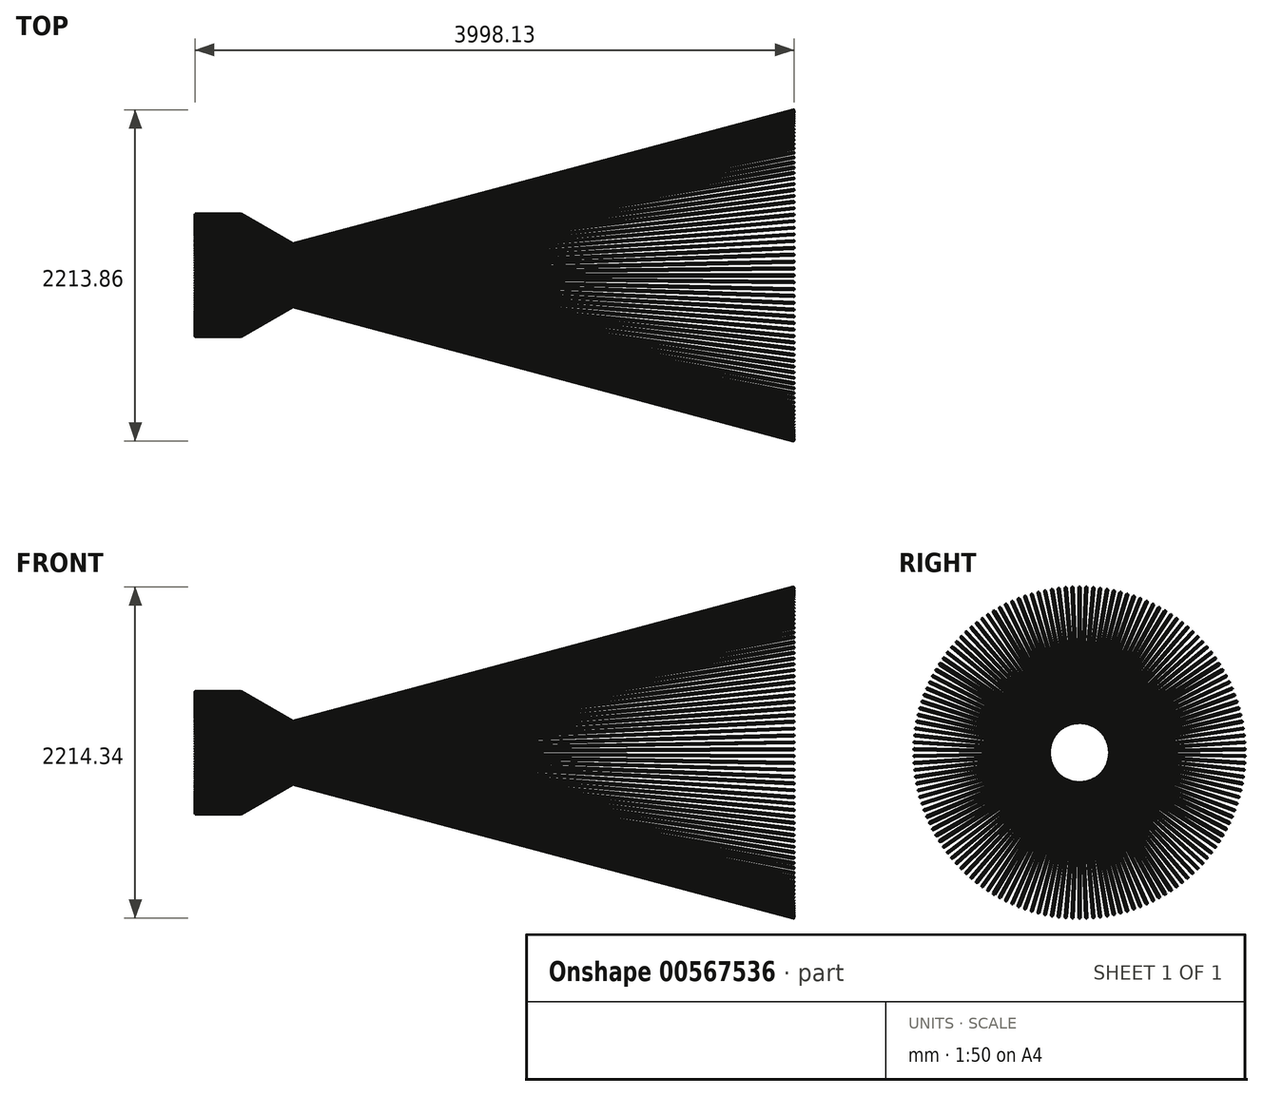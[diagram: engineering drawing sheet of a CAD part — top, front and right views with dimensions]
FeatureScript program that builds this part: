
annotation { "Feature Type Name" : "Feature", "Feature Type Description" : "" }
export const myFeature = defineFeature(function(context is Context, id is Id, definition is map)
    precondition{}
    {
        {
            var Q0;
            Q0=qCreatedBy(makeId("Right.planeOp"),FACE);
            var sketch = newSketch(context, id + "F0", { "sketchPlane" : qUnion([Q0])});
            skCircle(sketch, "E0", {"center": v(0, 405.5) * mm, "radius": 4.37 * mm});
            skSolve(sketch);
        }
        {
            var Q0;
            Q0=qCreatedBy(makeId("Front.planeOp"),FACE);
            var sketch = newSketch(context, id + "F1", { "sketchPlane" : qUnion([Q0])});
            skLineSegment(sketch, "E1", {"start": v(0, 400.9) * mm, "end": v(300, 400.9) * mm});
            skLineSegment(sketch, "E2", {"start": v(300, 400.9) * mm, "end": v(647, 200.56) * mm});
            skLineSegment(sketch, "E3", {"start": v(3998.18, 1098.5) * mm, "end": v(647, 200.56) * mm});
            skSolve(sketch);
        }
        {
            var Q0;
            Q0=makeQuery(id+"F0.imprint","IMPRINT",FACE,{"disambiguationData":[TD([[makeQuery(id+"F0.imprint","IMPRINT",EDGE,{"derivedFrom":sQuery(id+"F0.wireOp",EDGE,"E0")}),1.0]])]});
            var Q1;
            Q1=sQuery(id+"F1.wireOp",EDGE,"E1");
            var Q2;
            Q2=sQuery(id+"F1.wireOp",EDGE,"E2");
            var Q3;
            Q3=sQuery(id+"F1.wireOp",EDGE,"E3");
            sweep(context, id + "F2", {"profiles" : qUnion([Q0]), "path" : qUnion([Q1, Q2, Q3])});
        }
        {
            var Q0;
            Q0=qCreatedBy(makeId("Front.planeOp"),FACE);
            var sketch = newSketch(context, id + "F3", { "sketchPlane" : qUnion([Q0])});
            skLineSegment(sketch, "E4", {"start": v(0, 0) * mm, "end": v(74.42, 0) * mm});
            skSolve(sketch);
        }
        {
            var Q0;
            Q0=makeQuery(id+"F2.opSweep","SWEPT_BODY",BODY,{"disambiguationData":[OSD([sQuery(id+"F0.wireOp",EDGE,"E0"),sQuery(id+"F1.wireOp",EDGE,"E3")])]});
            var Q1;
            Q1=sQuery(id+"F3.wireOp",EDGE,"E4");
            circularPattern(context, id + "F4", {"entities" : qUnion([Q0]), "axis" : qUnion([Q1]), "angle" : 360 * degree, "instanceCount" : 150, "equalSpace" : true});
        }
        {
            var Q0;
            Q0 = qSketchRegion(id + "F1", true);
            var Q1;
            Q1 = qConstructionFilter(qBodyType(qCreatedBy(id + "F1" ,EDGE), BodyType.WIRE), ConstructionObject.NO);
            var Q2;
            Q2=sQuery(id+"F3.wireOp",EDGE,"E4");
            revolve(context, id + "F5", {"bodyType" : ToolBodyType.SURFACE, "entities" : qUnion([Q0]), "surfaceEntities" : qUnion([Q1]), "axis" : qUnion([Q2]), "revolveType" : RevolveType.FULL});
        }
    });
